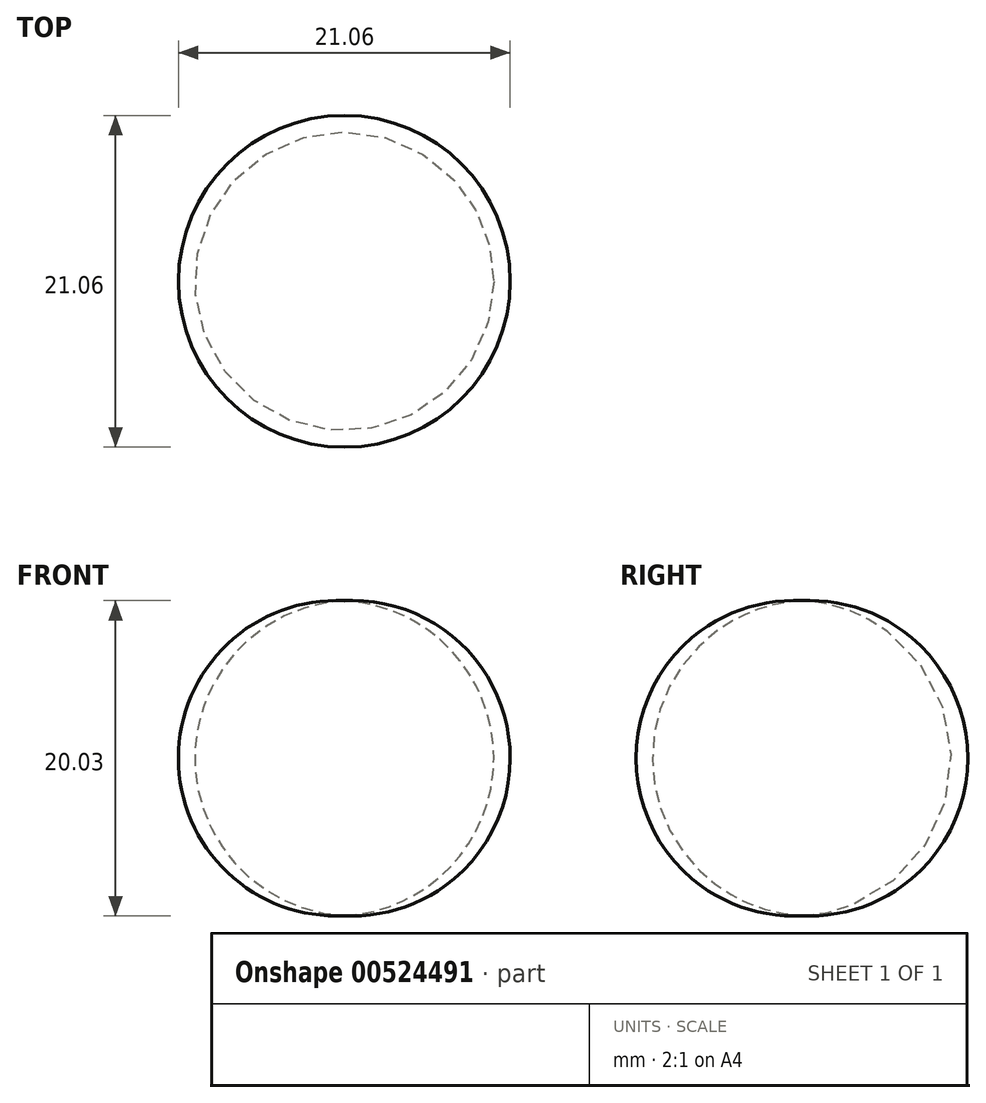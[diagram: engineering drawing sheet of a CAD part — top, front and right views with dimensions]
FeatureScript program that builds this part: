
annotation { "Feature Type Name" : "Feature", "Feature Type Description" : "" }
export const myFeature = defineFeature(function(context is Context, id is Id, definition is map)
    precondition{}
    {
        {
            var Q0;
            Q0=qCreatedBy(makeId("Front.planeOp"),FACE);
            var sketch = newSketch(context, id + "F0", { "sketchPlane" : qUnion([Q0])});
            skLineSegment(sketch, "E0", {"start": v(0, -9.77) * mm, "end": v(0, 10.23) * mm});
            skArc(sketch, "E1", {"start": v(0, 10.23) * mm, "mid": v(-10.53, 0.23) * mm, "end": v(0, -9.77) * mm});
            skSolve(sketch);
        }
        {
            var Q0;
            Q0=makeQuery(id+"F0.imprint","IMPRINT",FACE,{"disambiguationData":[TD([[makeQuery(id+"F0.imprint","IMPRINT",EDGE,{"derivedFrom":sQuery(id+"F0.wireOp",EDGE,"E0")}),1.0]])]});
            var Q1;
            Q1=sQuery(id+"F0.wireOp",EDGE,"E0");
            revolve(context, id + "F1", {"entities" : qUnion([Q0]), "axis" : qUnion([Q1]), "revolveType" : RevolveType.FULL});
        }
    });
